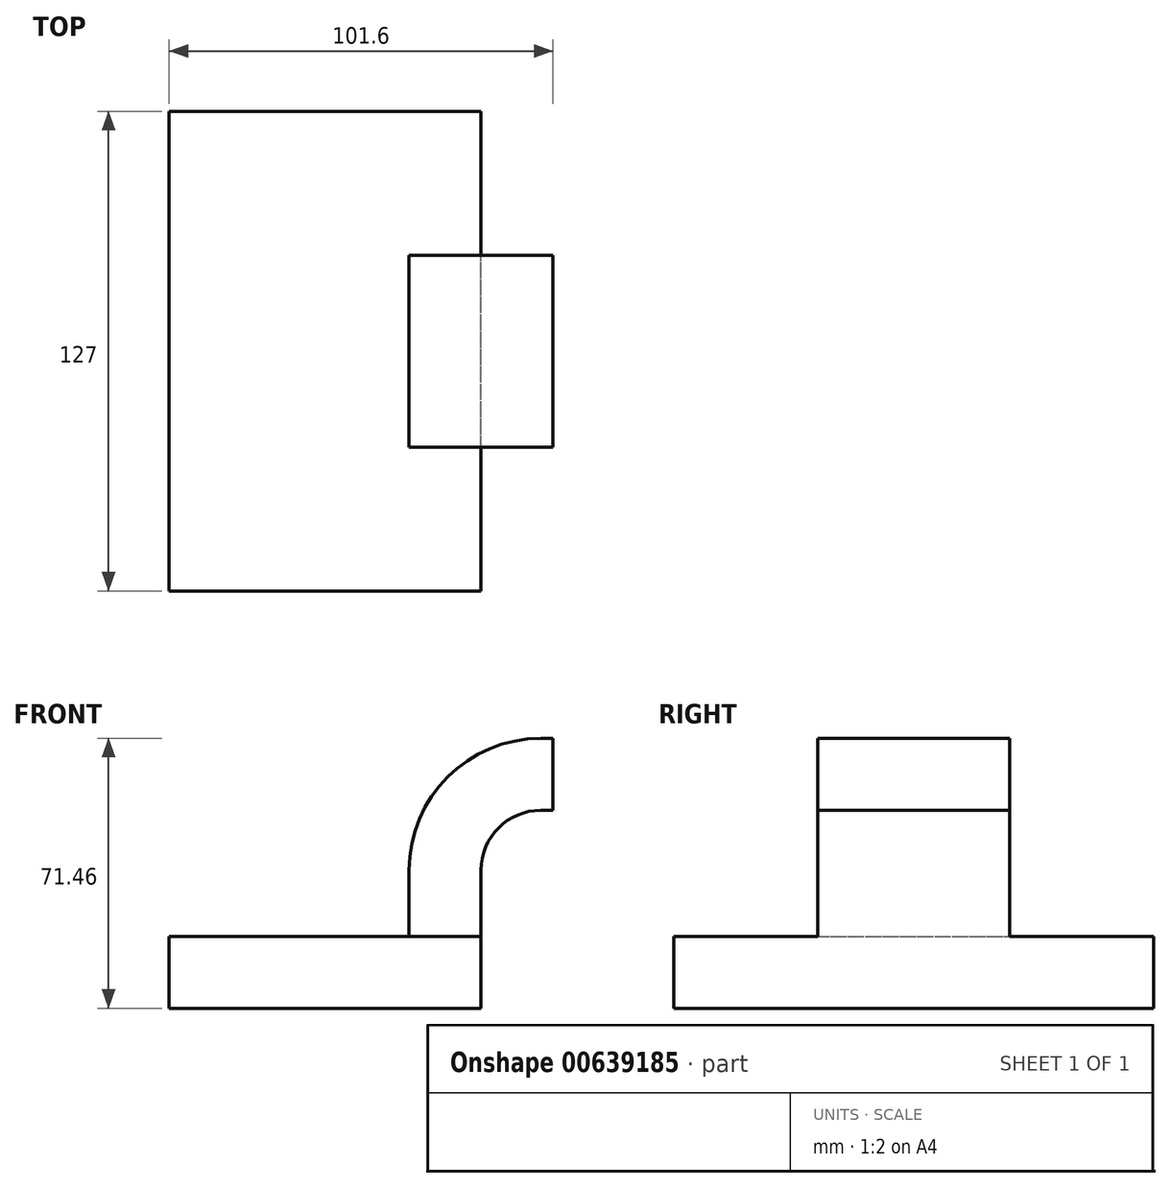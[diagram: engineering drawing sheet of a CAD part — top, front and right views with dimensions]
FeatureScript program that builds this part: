
annotation { "Feature Type Name" : "Feature", "Feature Type Description" : "" }
export const myFeature = defineFeature(function(context is Context, id is Id, definition is map)
    precondition{}
    {
        {
            var Q0;
            Q0=qCreatedBy(makeId("Front.planeOp"),FACE);
            var sketch = newSketch(context, id + "F0", { "sketchPlane" : qUnion([Q0])});
            skLineSegment(sketch, "E0.bottom", {"start": v(41.28, 9.53) * mm, "end": v(-41.28, 9.53) * mm});
            skLineSegment(sketch, "E0.top", {"start": v(41.28, -9.52) * mm, "end": v(-41.28, -9.52) * mm});
            skLineSegment(sketch, "E0.left", {"start": v(41.28, 9.53) * mm, "end": v(41.28, -9.52) * mm});
            skLineSegment(sketch, "E0.right", {"start": v(-41.28, 9.53) * mm, "end": v(-41.28, -9.52) * mm});
            skPoint(sketch, "E0.middle", {"position": v(0, 0) * mm});
            skLineSegment(sketch, "E1.bottom", {"start": v(111.12, 66.68) * mm, "end": v(60.32, 66.68) * mm});
            skLineSegment(sketch, "E1.top", {"start": v(111.12, 38.1) * mm, "end": v(60.32, 38.1) * mm});
            skLineSegment(sketch, "E1.left", {"start": v(111.12, 66.68) * mm, "end": v(111.12, 38.1) * mm});
            skLineSegment(sketch, "E1.right", {"start": v(60.32, 66.67) * mm, "end": v(60.32, 38.1) * mm});
            skPoint(sketch, "E1.middle", {"position": v(85.72, 52.39) * mm});
            skLineSegment(sketch, "E2", {"start": v(41.28, 9.53) * mm, "end": v(41.28, 27) * mm});
            skArc(sketch, "E3", {"start": v(41.27, 27) * mm, "mid": v(45.92, 38.23) * mm, "end": v(57.15, 42.88) * mm});
            skLineSegment(sketch, "E4", {"start": v(57.15, 42.88) * mm, "end": v(60.08, 42.88) * mm});
            skLineSegment(sketch, "E5.0", {"start": v(57.15, 61.93) * mm, "end": v(60.08, 61.93) * mm});
            skArc(sketch, "E5.1", {"start": v(22.22, 27) * mm, "mid": v(32.45, 51.7) * mm, "end": v(57.15, 61.93) * mm});
            skLineSegment(sketch, "E5.2", {"start": v(22.22, 9.53) * mm, "end": v(22.22, 27) * mm});
            skLineSegment(sketch, "E6", {"start": v(60.08, 61.93) * mm, "end": v(85.72, 61.93) * mm});
            skLineSegment(sketch, "E7", {"start": v(85.72, 61.93) * mm, "end": v(85.72, 42.97) * mm});
            skLineSegment(sketch, "E8", {"start": v(85.72, 42.97) * mm, "end": v(60.08, 42.88) * mm});
            skLineSegment(sketch, "E9", {"start": v(85.72, 66.68) * mm, "end": v(85.72, 38.1) * mm});
            skFitSpline(sketch, "E10", {"points": [v(-41.28, 9.52) * mm, v(57.15, 61.93) * mm], "startDerivative": vector(2.5, 82.6) * mm, "endDerivative": vector(142.4, 0) * mm});
            skSolve(sketch);
        }
        {
            var Q0;
            Q0=makeQuery(id+"F0.imprint","IMPRINT",FACE,{"disambiguationData":[TD([[makeQuery(id+"F0.imprint","IMPRINT",EDGE,{"derivedFrom":sQuery(id+"F0.wireOp",EDGE,"E0.top")}),-1.0]])]});
            extrude(context, id + "F1", {"entities" : qUnion([Q0]), "endBound" : BoundingType.SYMMETRIC, "depth" : 127 * mm, "offsetDistance" : 25.4 * mm});
        }
        {
            var Q0;
            {var subQ0=sQuery(id+"F0.wireOp",EDGE,"E2");Q0=makeQuery(id+"F0.imprint","IMPRINT",FACE,{"disambiguationData":[TD([[makeQuery(id+"F0.imprint","IMPRINT",EDGE,{"derivedFrom":subQ0}),1.0]])]});}
            extrude(context, id + "F2", {"entities" : qUnion([Q0]), "operationType" : NewBodyOperationType.ADD, "endBound" : BoundingType.SYMMETRIC, "depth" : 50.8 * mm, "offsetDistance" : 25.4 * mm});
        }
        {
            var Q0;
            Q0=makeQuery(id+"F0.imprint","IMPRINT",FACE,{"disambiguationData":[TD([[makeQuery(id+"F0.imprint","IMPRINT",EDGE,{"derivedFrom":sQuery(id+"F0.wireOp",EDGE,"E5.1")}),1.0]])]});
            extrude(context, id + "F3", {"entities" : qUnion([Q0]), "operationType" : NewBodyOperationType.ADD, "endBound" : BoundingType.SYMMETRIC, "depth" : 15.88 * mm, "offsetDistance" : 25.4 * mm});
        }
    });
